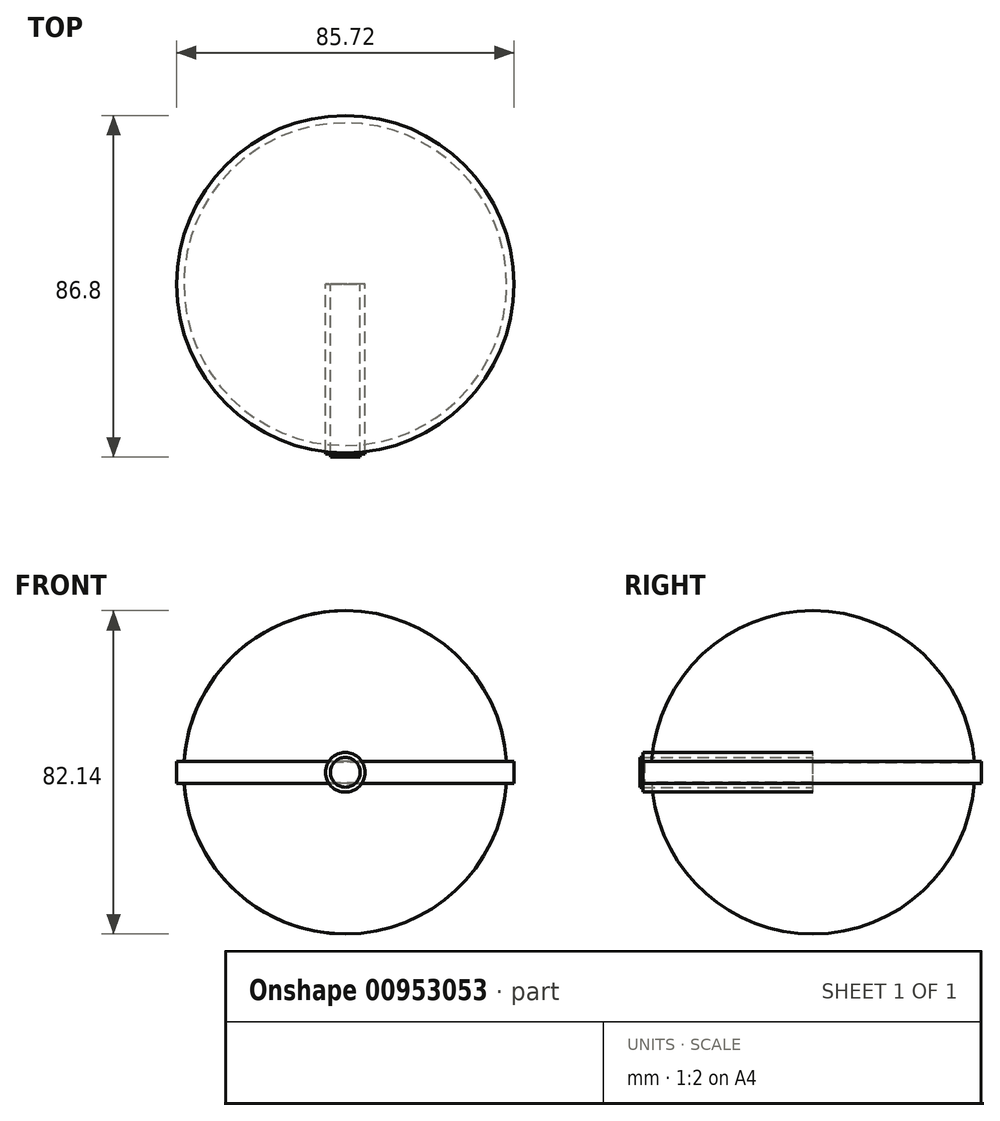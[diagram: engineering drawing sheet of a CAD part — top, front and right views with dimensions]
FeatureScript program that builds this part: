
annotation { "Feature Type Name" : "Feature", "Feature Type Description" : "" }
export const myFeature = defineFeature(function(context is Context, id is Id, definition is map)
    precondition{}
    {
        {
            var Q0;
            Q0=qCreatedBy(makeId("Front.planeOp"),FACE);
            var sketch = newSketch(context, id + "F0", { "sketchPlane" : qUnion([Q0])});
            skArc(sketch, "E0", {"start": v(0, -41.07) * mm, "mid": v(41.07, 0) * mm, "end": v(0, 41.07) * mm});
            skLineSegment(sketch, "E1", {"start": v(0, 41.07) * mm, "end": v(0, -41.07) * mm});
            skSolve(sketch);
        }
        {
            var Q0;
            Q0=makeQuery(id+"F0.imprint","IMPRINT",FACE,{"disambiguationData":[TD([[makeQuery(id+"F0.imprint","IMPRINT",EDGE,{"derivedFrom":sQuery(id+"F0.wireOp",EDGE,"E0")}),1.0]])]});
            var Q1;
            Q1=sQuery(id+"F0.wireOp",EDGE,"E1");
            revolve(context, id + "F1", {"surfaceOperationType" : NewSurfaceOperationType.NEW, "entities" : qUnion([Q0]), "axis" : qUnion([Q1]), "revolveType" : RevolveType.FULL});
        }
        {
            var Q0;
            Q0=qCreatedBy(makeId("Front.planeOp"),FACE);
            cPlane(context, id + "F2", {"entities" : qUnion([Q0]), "cplaneType" : CPlaneType.OFFSET, "offset" : 74.68 * mm, "width" : 152.4 * mm, "height" : 152.4 * mm});
        }
        {
            var Q0;
            Q0=qCreatedBy(id+"F2.planeOp",FACE);
            var sketch = newSketch(context, id + "F3", { "sketchPlane" : qUnion([Q0])});
            skLineSegment(sketch, "E2.bottom", {"start": v(45.48, -2.5) * mm, "end": v(-45.48, -2.5) * mm});
            skLineSegment(sketch, "E2.top", {"start": v(45.48, 2.5) * mm, "end": v(-45.48, 2.5) * mm});
            skLineSegment(sketch, "E2.left", {"start": v(45.48, -2.5) * mm, "end": v(45.48, 2.5) * mm});
            skLineSegment(sketch, "E2.right", {"start": v(-45.48, -2.5) * mm, "end": v(-45.48, 2.5) * mm});
            skPoint(sketch, "E2.middle", {"position": v(0, 0) * mm});
            skSolve(sketch);
        }
        {
            var Q0;
            Q0=makeQuery(id+"F3.imprint","IMPRINT",FACE,{"disambiguationData":[TD([[makeQuery(id+"F3.imprint","IMPRINT",EDGE,{"derivedFrom":sQuery(id+"F3.wireOp",EDGE,"E2.bottom")}),-1.0]])]});
            extrude(context, id + "F4", {"entities" : qUnion([Q0]), "operationType" : NewBodyOperationType.REMOVE, "oppositeDirection" : true, "depth" : 191 * mm, "offsetDistance" : 25.4 * mm});
        }
        {
            var Q0;
            Q0=qCreatedBy(makeId("Top.planeOp"),FACE);
            var sketch = newSketch(context, id + "F5", { "sketchPlane" : qUnion([Q0])});
            skCircle(sketch, "E3", {"center": v(0, 0) * mm, "radius": 42.86 * mm});
            skSolve(sketch);
        }
        {
            var Q0;
            Q0=makeQuery(id+"F5.imprint","IMPRINT",FACE,{"disambiguationData":[TD([[makeQuery(id+"F5.imprint","IMPRINT",EDGE,{"derivedFrom":sQuery(id+"F5.wireOp",EDGE,"E3")}),1.0]])]});
            extrude(context, id + "F6", {"entities" : qUnion([Q0]), "endBound" : BoundingType.SYMMETRIC, "depth" : 5.6 * mm, "offsetDistance" : 25.4 * mm});
        }
        {
            var Q0;
            Q0=qCreatedBy(makeId("Front.planeOp"),FACE);
            var sketch = newSketch(context, id + "F7", { "sketchPlane" : qUnion([Q0])});
            skCircle(sketch, "E4", {"center": v(0, 0) * mm, "radius": 3.79 * mm});
            skSolve(sketch);
        }
        {
            var Q0;
            Q0 = qSketchRegion(id + "F7", true);
            extrude(context, id + "F8", {"entities" : qUnion([Q0]), "depth" : 43.94 * mm, "offsetDistance" : 25.4 * mm});
        }
        {
            var Q0;
            Q0=qCreatedBy(makeId("Front.planeOp"),FACE);
            var sketch = newSketch(context, id + "F9", { "sketchPlane" : qUnion([Q0])});
            skCircle(sketch, "E5", {"center": v(0, 0) * mm, "radius": 5.04 * mm});
            skSolve(sketch);
        }
        {
            var Q0;
            Q0 = qSketchRegion(id + "F9", true);
            extrude(context, id + "F10", {"entities" : qUnion([Q0]), "depth" : 43.18 * mm, "offsetDistance" : 25.4 * mm});
        }
    });
